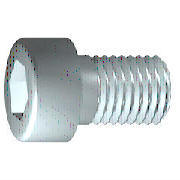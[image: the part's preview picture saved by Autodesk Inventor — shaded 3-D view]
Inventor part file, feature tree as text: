
AUTODESK INVENTOR PART (.ipt)
format: ipt  version: 2020 (Build 240168000, 168)  size: 189,440 bytes
history: native  units: mm (DEFAULTED — no unit token found)
features: sketch x2, other x1, extrude x1, plane x1, fillet x1
ambient origin geometry x7: Origin, YZ Plane, XY Plane, X Axis, Y Axis, Z Axis, Center Point
bodies: Solid1 (feature_tree)
feature tree (6):
  other  "Bryła"
  extrude  "Szczelina"  Depth=16.5mm
  plane  "Work Plane1"
  fillet  "Fillet2"  Radius=0.306825mm
  sketch  "Szkic1"
  sketch  "Szkic2"
